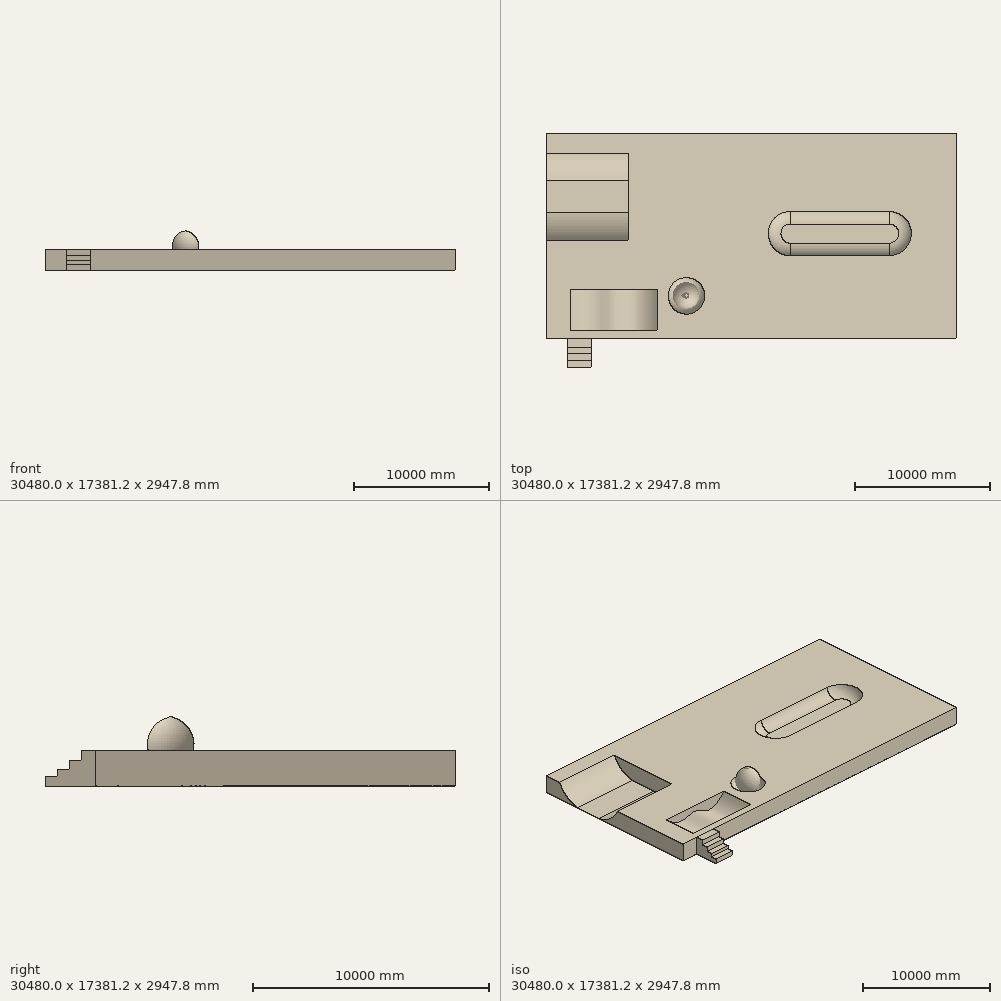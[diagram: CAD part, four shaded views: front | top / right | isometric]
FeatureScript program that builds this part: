
annotation { "Feature Type Name" : "Feature", "Feature Type Description" : "" }
export const myFeature = defineFeature(function(context is Context, id is Id, definition is map)
    precondition{}
    {
        {
            var Q0;
            Q0=qCreatedBy(makeId("Top.planeOp"),FACE);
            var sketch = newSketch(context, id + "F0", { "sketchPlane" : qUnion([Q0])});
            skLineSegment(sketch, "E0.bottom", {"start": v(0, 0) * mm, "end": v(30480, 0) * mm});
            skLineSegment(sketch, "E0.top", {"start": v(0, 15240) * mm, "end": v(30480, 15240) * mm});
            skLineSegment(sketch, "E0.left", {"start": v(0, 0) * mm, "end": v(0, 15240) * mm});
            skLineSegment(sketch, "E0.right", {"start": v(30480, 0) * mm, "end": v(30480, 15240) * mm});
            skLineSegment(sketch, "E1.bottom", {"start": v(15240, 15240) * mm, "end": v(8833.37, 15240) * mm});
            skLineSegment(sketch, "E1.top", {"start": v(15240, 15240) * mm, "end": v(8833.37, 15240) * mm});
            skLineSegment(sketch, "E1.left", {"start": v(15240, 15240) * mm, "end": v(15240, 15240) * mm});
            skLineSegment(sketch, "E1.right", {"start": v(8833.37, 15240) * mm, "end": v(8833.37, 15240) * mm});
            skSolve(sketch);
        }
        {
            var Q0;
            Q0=makeQuery(id+"F0.imprint","IMPRINT",FACE,{"disambiguationData":[TD([[makeQuery(id+"F0.imprint","IMPRINT",EDGE,{"derivedFrom":sQuery(id+"F0.wireOp",EDGE,"E0.bottom")}),1.0]])]});
            extrude(context, id + "F1", {"entities" : qUnion([Q0]), "depth" : 1524 * mm});
        }
        {
            var Q0;
            Q0=makeQuery(id+"F0.imprint","IMPRINT",FACE,{"disambiguationData":[TD([[makeQuery(id+"F0.imprint","IMPRINT",EDGE,{"derivedFrom":sQuery(id+"F0.wireOp",EDGE,"E0.bottom")}),1.0]])]});
            extrude(context, id + "F2", {"entities" : qUnion([Q0]), "depth" : 30.48 * mm});
        }
        {
            var Q0;
            Q0=makeQuery(id+"F1.opExtrude","SWEPT_FACE",FACE,{"disambiguationData":[OSD([sQuery(id+"F0.wireOp",EDGE,"E0.bottom")])]});
            var sketch = newSketch(context, id + "F3", { "sketchPlane" : qUnion([Q0])});
            skFitSpline(sketch, "E2", {"points": [v(1766.2, 1524) * mm, v(2729.25, 906.23) * mm, v(3813.85, 737.93) * mm, v(5001.3, 990.38) * mm, v(5973.7, 644.42) * mm, v(6768.45, 485.47) * mm, v(7675.4, 915.58) * mm, v(8217.7, 1524) * mm], "startDerivative": vector(6115.8, -4583.84) * mm, "endDerivative": vector(3663.6, 4921.68) * mm});
            skLineSegment(sketch, "E3", {"start": v(1766.2, 1524) * mm, "end": v(8217.7, 1524) * mm});
            skSolve(sketch);
        }
        {
            var Q0;
            Q0=makeQuery(id+"F3.imprint","IMPRINT",FACE,{"disambiguationData":[TD([[makeQuery(id+"F3.imprint","IMPRINT",EDGE,{"derivedFrom":sQuery(id+"F3.wireOp",EDGE,"E2")}),1.0]])]});
            extrude(context, id + "F4", {"entities" : qUnion([Q0]), "depth" : 3048 * mm});
        }
        {
            var Q0;
            Q0=makeQuery(id+"F4.opExtrude","SWEPT_BODY",BODY,{"disambiguationData":[OSD([sQuery(id+"F3.wireOp",EDGE,"E2"),sQuery(id+"F3.wireOp",EDGE,"E3")])]});
            transform(context, id + "F5", {"entities" : qUnion([Q0]), "transformType" : TransformType.TRANSLATION_3D, "dx" : 0 * mm, "dy" : 3657.6 * mm, "dz" : 0 * mm, "makeCopy" : false});
        }
        {
            var Q0;
            Q0=makeQuery(id+"F4.opExtrude","SWEPT_BODY",BODY,{"disambiguationData":[OSD([sQuery(id+"F3.wireOp",EDGE,"E2"),sQuery(id+"F3.wireOp",EDGE,"E3")])]});
            var Q1;
            Q1=makeQuery(id+"F1.opExtrude","SWEPT_BODY",BODY,{"disambiguationData":[OSD([sQuery(id+"F0.wireOp",EDGE,"E0.bottom"),sQuery(id+"F0.wireOp",EDGE,"E0.top"),sQuery(id+"F0.wireOp",EDGE,"E0.left"),sQuery(id+"F0.wireOp",EDGE,"E0.right"),sQuery(id+"F0.wireOp",EDGE,"E1.top")])]});
            booleanBodies(context, id + "F6", {"operationType" : BooleanOperationType.SUBTRACTION, "tools" : qUnion([Q0]), "targets" : qUnion([Q1])});
        }
        {
            var Q0;
            Q0=makeQuery(id+"F1.opExtrude","SWEPT_FACE",FACE,{"disambiguationData":[OSD([sQuery(id+"F0.wireOp",EDGE,"E0.bottom")])]});
            var sketch = newSketch(context, id + "F7", { "sketchPlane" : qUnion([Q0])});
            skArc(sketch, "E4", {"start": v(9059.2, 1524) * mm, "mid": v(9550.27, 787.43) * mm, "end": v(10414.95, 597.67) * mm});
            skLineSegment(sketch, "E5", {"start": v(10414.95, 597.67) * mm, "end": v(10414.95, 1524) * mm});
            skLineSegment(sketch, "E6", {"start": v(10414.95, 1524) * mm, "end": v(9059.2, 1524) * mm});
            skSolve(sketch);
        }
        {
            var Q0;
            Q0=makeQuery(id+"F7.imprint","IMPRINT",FACE,{"disambiguationData":[TD([[makeQuery(id+"F7.imprint","IMPRINT",EDGE,{"derivedFrom":sQuery(id+"F7.wireOp",EDGE,"E4")}),1.0]])]});
            var Q1;
            Q1=sQuery(id+"F7.wireOp",EDGE,"E5");
            revolve(context, id + "F8", {"entities" : qUnion([Q0]), "axis" : qUnion([Q1]), "revolveType" : RevolveType.FULL});
        }
        {
            var Q0;
            Q0=makeQuery(id+"F8.opRevolve","SWEPT_BODY",BODY,{"disambiguationData":[OSD([sQuery(id+"F7.wireOp",EDGE,"E4"),sQuery(id+"F7.wireOp",EDGE,"E5"),sQuery(id+"F7.wireOp",EDGE,"E6")])]});
            transform(context, id + "F9", {"entities" : qUnion([Q0]), "transformType" : TransformType.TRANSLATION_3D, "dx" : 0 * mm, "dy" : 3169.92 * mm, "dz" : 0 * mm, "makeCopy" : false});
        }
        {
            var Q0;
            Q0=makeQuery(id+"F8.opRevolve","SWEPT_BODY",BODY,{"disambiguationData":[OSD([sQuery(id+"F7.wireOp",EDGE,"E4"),sQuery(id+"F7.wireOp",EDGE,"E5"),sQuery(id+"F7.wireOp",EDGE,"E6")])]});
            var Q1;
            Q1=makeQuery(id+"F1.opExtrude","SWEPT_BODY",BODY,{"disambiguationData":[OSD([sQuery(id+"F0.wireOp",EDGE,"E0.bottom"),sQuery(id+"F0.wireOp",EDGE,"E0.top"),sQuery(id+"F0.wireOp",EDGE,"E0.left"),sQuery(id+"F0.wireOp",EDGE,"E0.right"),sQuery(id+"F0.wireOp",EDGE,"E1.top")])]});
            booleanBodies(context, id + "F10", {"operationType" : BooleanOperationType.SUBTRACTION, "tools" : qUnion([Q0]), "targets" : qUnion([Q1])});
        }
        {
            var Q0;
            Q0=makeQuery(id+"F1.opExtrude","SWEPT_FACE",FACE,{"disambiguationData":[OSD([sQuery(id+"F0.wireOp",EDGE,"E0.bottom")])]});
            var sketch = newSketch(context, id + "F11", { "sketchPlane" : qUnion([Q0])});
            skLineSegment(sketch, "E7", {"start": v(1541.8, 1524) * mm, "end": v(2177.6, 1524) * mm});
            skLineSegment(sketch, "E8", {"start": v(2177.6, 1524) * mm, "end": v(2177.6, 1083.88) * mm});
            skLineSegment(sketch, "E9", {"start": v(2177.6, 1083.88) * mm, "end": v(2673.15, 1083.88) * mm});
            skLineSegment(sketch, "E10", {"start": v(2673.15, 1083.88) * mm, "end": v(2673.15, 700.52) * mm});
            skLineSegment(sketch, "E11", {"start": v(2673.15, 700.52) * mm, "end": v(3178.05, 700.52) * mm});
            skLineSegment(sketch, "E12", {"start": v(3178.05, 700.52) * mm, "end": v(3178.05, 410.67) * mm});
            skLineSegment(sketch, "E13", {"start": v(3178.05, 410.67) * mm, "end": v(3682.95, 410.67) * mm});
            skLineSegment(sketch, "E14", {"start": v(3682.95, 410.67) * mm, "end": v(3682.95, 0) * mm});
            skLineSegment(sketch, "E15", {"start": v(3682.95, 0) * mm, "end": v(1541.8, 0) * mm});
            skLineSegment(sketch, "E16", {"start": v(1541.8, 0) * mm, "end": v(1541.8, 1524) * mm});
            skSolve(sketch);
        }
        {
            var Q0;
            Q0=makeQuery(id+"F11.imprint","IMPRINT",FACE,{"disambiguationData":[TD([[makeQuery(id+"F11.imprint","IMPRINT",EDGE,{"derivedFrom":sQuery(id+"F11.wireOp",EDGE,"E7")}),-1.0]])]});
            extrude(context, id + "F12", {"entities" : qUnion([Q0]), "depth" : 1828.8 * mm});
        }
        {
            var Q0;
            Q0=makeQuery(id+"F12.opExtrude","SWEPT_BODY",BODY,{"disambiguationData":[OSD([sQuery(id+"F11.wireOp",EDGE,"E7"),sQuery(id+"F11.wireOp",EDGE,"E8"),sQuery(id+"F11.wireOp",EDGE,"E9"),sQuery(id+"F11.wireOp",EDGE,"E10"),sQuery(id+"F11.wireOp",EDGE,"E11"),sQuery(id+"F11.wireOp",EDGE,"E12"),sQuery(id+"F11.wireOp",EDGE,"E13"),sQuery(id+"F11.wireOp",EDGE,"E14"),sQuery(id+"F11.wireOp",EDGE,"E15"),sQuery(id+"F11.wireOp",EDGE,"E16")])]});
            var Q1;
            Q1=makeQuery(id+"F12.opExtrude","CAP_EDGE",EDGE,{"disambiguationData":[OSD([sQuery(id+"F11.wireOp",EDGE,"E16")])],"isStart":false});
            transform(context, id + "F13", {"entities" : qUnion([Q0]), "transformType" : TransformType.ROTATION, "transformAxis" : qUnion([Q1]), "angle" : 90 * degree, "oppositeDirection" : true, "makeCopy" : false});
        }
        {
            var Q0;
            Q0=makeQuery(id+"F12.opExtrude","SWEPT_BODY",BODY,{"disambiguationData":[OSD([sQuery(id+"F11.wireOp",EDGE,"E7"),sQuery(id+"F11.wireOp",EDGE,"E8"),sQuery(id+"F11.wireOp",EDGE,"E9"),sQuery(id+"F11.wireOp",EDGE,"E10"),sQuery(id+"F11.wireOp",EDGE,"E11"),sQuery(id+"F11.wireOp",EDGE,"E12"),sQuery(id+"F11.wireOp",EDGE,"E13"),sQuery(id+"F11.wireOp",EDGE,"E14"),sQuery(id+"F11.wireOp",EDGE,"E15"),sQuery(id+"F11.wireOp",EDGE,"E16")])]});
            transform(context, id + "F14", {"entities" : qUnion([Q0]), "transformType" : TransformType.TRANSLATION_3D, "dx" : 0 * mm, "dy" : 1828.8 * mm, "dz" : 0 * mm, "makeCopy" : false});
        }
        {
            var Q0;
            Q0=makeQuery(id+"F1.opExtrude","SWEPT_FACE",FACE,{"disambiguationData":[OSD([sQuery(id+"F0.wireOp",EDGE,"E0.left")])]});
            var sketch = newSketch(context, id + "F15", { "sketchPlane" : qUnion([Q0])});
            skArc(sketch, "E17", {"start": v(-13764.62, 1524) * mm, "mid": v(-12838.56, 468.78) * mm, "end": v(-11515.18, 0) * mm});
            skLineSegment(sketch, "E18", {"start": v(-11515.18, 0) * mm, "end": v(-9732.6, 0) * mm});
            skArc(sketch, "E19", {"start": v(-9732.6, 0) * mm, "mid": v(-8302.99, 412.76) * mm, "end": v(-7313.39, 1524) * mm});
            skLineSegment(sketch, "E20", {"start": v(-13764.62, 1524) * mm, "end": v(-7313.39, 1524) * mm});
            skSolve(sketch);
        }
        {
            var Q0;
            Q0=makeQuery(id+"F15.imprint","IMPRINT",FACE,{"disambiguationData":[TD([[makeQuery(id+"F15.imprint","IMPRINT",EDGE,{"derivedFrom":sQuery(id+"F15.wireOp",EDGE,"E17")}),1.0]])]});
            extrude(context, id + "F16", {"entities" : qUnion([Q0]), "depth" : 9144 * mm});
        }
        {
            var Q0;
            Q0=makeQuery(id+"F16.opExtrude","SWEPT_BODY",BODY,{"disambiguationData":[OSD([sQuery(id+"F15.wireOp",EDGE,"E17"),sQuery(id+"F15.wireOp",EDGE,"E18"),sQuery(id+"F15.wireOp",EDGE,"E19"),sQuery(id+"F15.wireOp",EDGE,"E20")])]});
            transform(context, id + "F17", {"entities" : qUnion([Q0]), "transformType" : TransformType.TRANSLATION_3D, "dx" : 6096 * mm, "dy" : 0 * mm, "dz" : 0 * mm, "makeCopy" : false});
        }
        {
            var Q0;
            Q0=makeQuery(id+"F16.opExtrude","SWEPT_BODY",BODY,{"disambiguationData":[OSD([sQuery(id+"F15.wireOp",EDGE,"E17"),sQuery(id+"F15.wireOp",EDGE,"E18"),sQuery(id+"F15.wireOp",EDGE,"E19"),sQuery(id+"F15.wireOp",EDGE,"E20")])]});
            var Q1;
            Q1=makeQuery(id+"F1.opExtrude","SWEPT_BODY",BODY,{"disambiguationData":[OSD([sQuery(id+"F0.wireOp",EDGE,"E0.bottom"),sQuery(id+"F0.wireOp",EDGE,"E0.top"),sQuery(id+"F0.wireOp",EDGE,"E0.left"),sQuery(id+"F0.wireOp",EDGE,"E0.right"),sQuery(id+"F0.wireOp",EDGE,"E1.top")])]});
            booleanBodies(context, id + "F18", {"operationType" : BooleanOperationType.SUBTRACTION, "tools" : qUnion([Q0]), "targets" : qUnion([Q1])});
        }
        {
            var Q0;
            Q0=qCreatedBy(makeId("Top.planeOp"),FACE);
            var sketch = newSketch(context, id + "F19", { "sketchPlane" : qUnion([Q0])});
            skLineSegment(sketch, "E21.bottom", {"start": v(6735.13, 5312.69) * mm, "end": v(14088.69, 5312.69) * mm});
            skLineSegment(sketch, "E21.top", {"start": v(6735.13, 1992.44) * mm, "end": v(14088.69, 1992.44) * mm});
            skArc(sketch, "E22", {"start": v(6735.13, 5312.69) * mm, "mid": v(5075, 3652.57) * mm, "end": v(6735.13, 1992.44) * mm});
            skArc(sketch, "E23", {"start": v(14088.69, 1992.44) * mm, "mid": v(15748.81, 3652.57) * mm, "end": v(14088.69, 5312.69) * mm});
            skSolve(sketch);
        }
        {
            var Q0;
            Q0=makeQuery(id+"F19.imprint","IMPRINT",FACE,{"disambiguationData":[TD([[makeQuery(id+"F19.imprint","IMPRINT",EDGE,{"derivedFrom":sQuery(id+"F19.wireOp",EDGE,"E21.bottom")}),-1.0]])]});
            extrude(context, id + "F20", {"entities" : qUnion([Q0]), "depth" : 1219.2 * mm});
        }
        {
            var Q0;
            Q0=makeQuery(id+"F20.opExtrude","CAP_EDGE",EDGE,{"disambiguationData":[OSD([sQuery(id+"F19.wireOp",EDGE,"E22")])],"isStart":true});
            var Q1;
            Q1=makeQuery(id+"F20.opExtrude","CAP_EDGE",EDGE,{"disambiguationData":[OSD([sQuery(id+"F19.wireOp",EDGE,"E21.top")])],"isStart":true});
            var Q2;
            Q2=makeQuery(id+"F20.opExtrude","CAP_EDGE",EDGE,{"disambiguationData":[OSD([sQuery(id+"F19.wireOp",EDGE,"E23")])],"isStart":true});
            var Q3;
            Q3=makeQuery(id+"F20.opExtrude","CAP_EDGE",EDGE,{"disambiguationData":[OSD([sQuery(id+"F19.wireOp",EDGE,"E21.bottom")])],"isStart":true});
            var Q4;
            Q4=makeQuery(id+"F20.opExtrude","CAP_FACE",FACE,{"disambiguationData":[OSD([sQuery(id+"F19.wireOp",EDGE,"E21.bottom"),sQuery(id+"F19.wireOp",EDGE,"E21.top"),sQuery(id+"F19.wireOp",EDGE,"E22"),sQuery(id+"F19.wireOp",EDGE,"E23")])],"isStart":true});
            fillet(context, id + "F21", {"entities" : qUnion([Q0, Q1, Q2, Q3, Q4]), "radius" : 956.6 * mm, "tangentPropagation" : true, "allowEdgeOverflow" : false});
        }
        {
            var Q0;
            Q0=makeQuery(id+"F20.opExtrude","SWEPT_BODY",BODY,{"disambiguationData":[OSD([sQuery(id+"F19.wireOp",EDGE,"E21.bottom"),sQuery(id+"F19.wireOp",EDGE,"E21.top"),sQuery(id+"F19.wireOp",EDGE,"E22"),sQuery(id+"F19.wireOp",EDGE,"E23")])]});
            transform(context, id + "F22", {"entities" : qUnion([Q0]), "transformType" : TransformType.TRANSLATION_3D, "dx" : 11399.52 * mm, "dy" : 4145.28 * mm, "dz" : 762 * mm, "makeCopy" : false});
        }
        {
            var Q0;
            Q0=makeQuery(id+"F20.opExtrude","SWEPT_BODY",BODY,{"disambiguationData":[OSD([sQuery(id+"F19.wireOp",EDGE,"E21.bottom"),sQuery(id+"F19.wireOp",EDGE,"E21.top"),sQuery(id+"F19.wireOp",EDGE,"E22"),sQuery(id+"F19.wireOp",EDGE,"E23")])]});
            var Q1;
            Q1=makeQuery(id+"F1.opExtrude","SWEPT_BODY",BODY,{"disambiguationData":[OSD([sQuery(id+"F0.wireOp",EDGE,"E0.bottom"),sQuery(id+"F0.wireOp",EDGE,"E0.top"),sQuery(id+"F0.wireOp",EDGE,"E0.left"),sQuery(id+"F0.wireOp",EDGE,"E0.right"),sQuery(id+"F0.wireOp",EDGE,"E1.top")])]});
            booleanBodies(context, id + "F23", {"operationType" : BooleanOperationType.SUBTRACTION, "tools" : qUnion([Q0]), "targets" : qUnion([Q1])});
        }
    });
